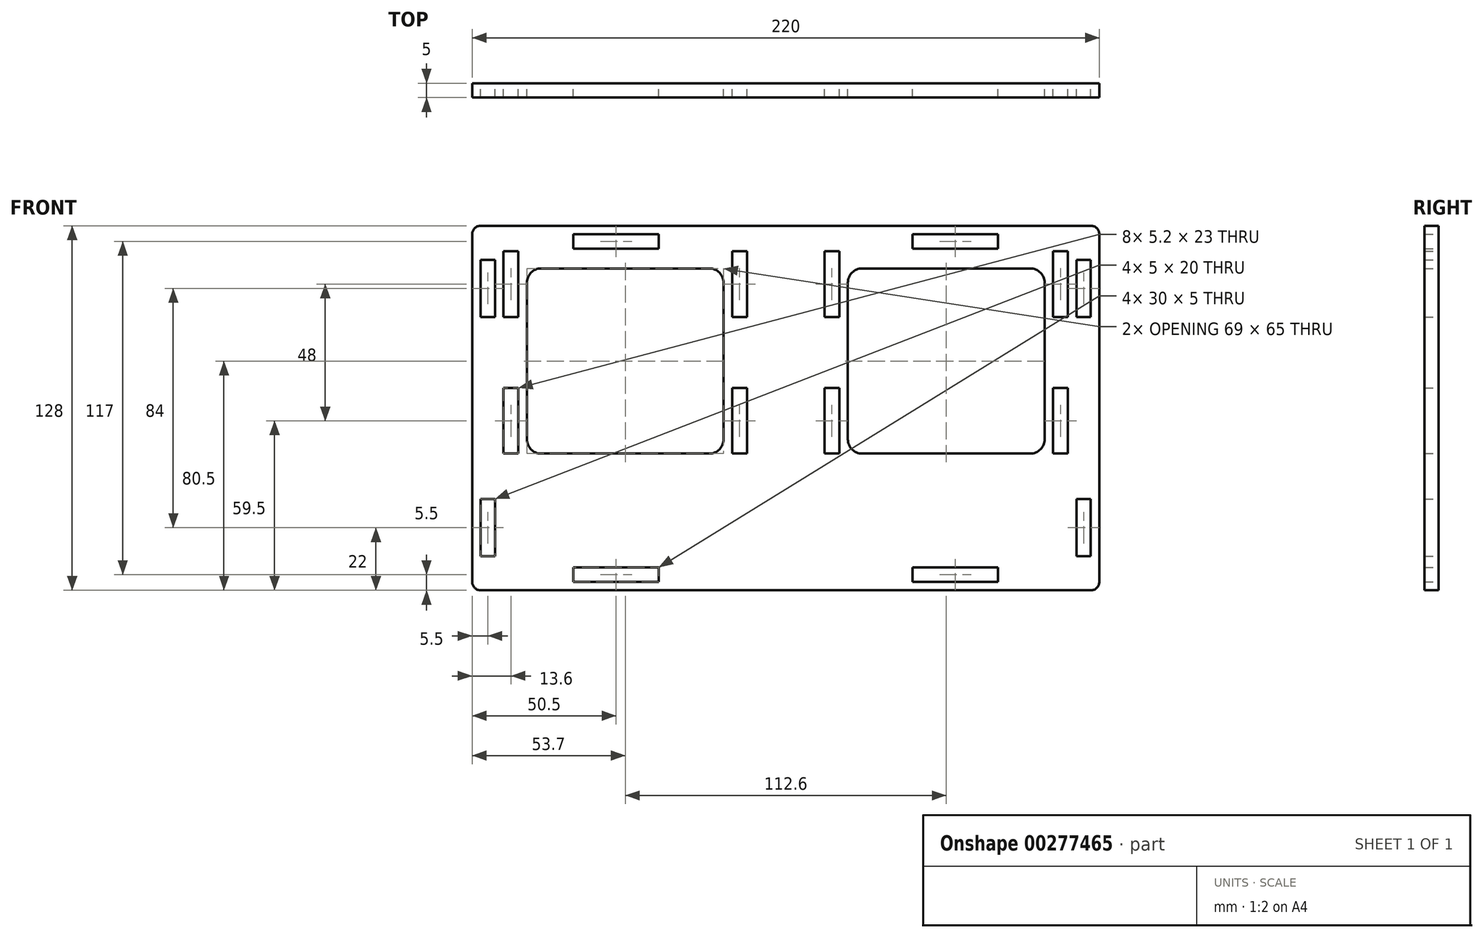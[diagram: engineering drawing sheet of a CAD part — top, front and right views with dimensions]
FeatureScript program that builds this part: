
annotation { "Feature Type Name" : "Feature", "Feature Type Description" : "" }
export const myFeature = defineFeature(function(context is Context, id is Id, definition is map)
    precondition{}
    {
        {
            var Q0;
            Q0=qCreatedBy(makeId("Front.planeOp"),FACE);
            var sketch = newSketch(context, id + "F0", { "sketchPlane" : qUnion([Q0])});
            skLineSegment(sketch, "E0.bottom", {"start": v(-107, 64) * mm, "end": v(107, 64) * mm});
            skLineSegment(sketch, "E0.top", {"start": v(-107, -64) * mm, "end": v(107, -64) * mm});
            skLineSegment(sketch, "E0.left", {"start": v(-110, 61) * mm, "end": v(-110, -61) * mm});
            skLineSegment(sketch, "E0.right", {"start": v(110, 61) * mm, "end": v(110, -61) * mm});
            skLineSegment(sketch, "E1.bottom", {"start": v(-107, 52) * mm, "end": v(-102, 52) * mm});
            skLineSegment(sketch, "E1.top", {"start": v(-107, 32) * mm, "end": v(-102, 32) * mm});
            skLineSegment(sketch, "E1.left", {"start": v(-107, 52) * mm, "end": v(-107, 32) * mm});
            skLineSegment(sketch, "E1.right", {"start": v(-102, 52) * mm, "end": v(-102, 32) * mm});
            skLineSegment(sketch, "E2.bottom", {"start": v(-107, -32) * mm, "end": v(-102, -32) * mm});
            skLineSegment(sketch, "E2.top", {"start": v(-107, -52) * mm, "end": v(-102, -52) * mm});
            skLineSegment(sketch, "E2.left", {"start": v(-107, -32) * mm, "end": v(-107, -52) * mm});
            skLineSegment(sketch, "E2.right", {"start": v(-102, -32) * mm, "end": v(-102, -52) * mm});
            skLineSegment(sketch, "E3.bottom", {"start": v(102, -32) * mm, "end": v(107, -32) * mm});
            skLineSegment(sketch, "E3.top", {"start": v(102, -52) * mm, "end": v(107, -52) * mm});
            skLineSegment(sketch, "E3.left", {"start": v(102, -32) * mm, "end": v(102, -52) * mm});
            skLineSegment(sketch, "E3.right", {"start": v(107, -32) * mm, "end": v(107, -52) * mm});
            skLineSegment(sketch, "E4.bottom", {"start": v(102, 52) * mm, "end": v(107, 52) * mm});
            skLineSegment(sketch, "E4.top", {"start": v(102, 32) * mm, "end": v(107, 32) * mm});
            skLineSegment(sketch, "E4.left", {"start": v(102, 52) * mm, "end": v(102, 32) * mm});
            skLineSegment(sketch, "E4.right", {"start": v(107, 52) * mm, "end": v(107, 32) * mm});
            skLineSegment(sketch, "E5.bottom", {"start": v(-74.5, 61) * mm, "end": v(-44.5, 61) * mm});
            skLineSegment(sketch, "E5.top", {"start": v(-74.5, 56) * mm, "end": v(-44.5, 56) * mm});
            skLineSegment(sketch, "E5.left", {"start": v(-74.5, 61) * mm, "end": v(-74.5, 56) * mm});
            skLineSegment(sketch, "E5.right", {"start": v(-44.5, 61) * mm, "end": v(-44.5, 56) * mm});
            skLineSegment(sketch, "E6.bottom", {"start": v(44.5, 61) * mm, "end": v(74.5, 61) * mm});
            skLineSegment(sketch, "E6.top", {"start": v(44.5, 56) * mm, "end": v(74.5, 56) * mm});
            skLineSegment(sketch, "E6.left", {"start": v(44.5, 61) * mm, "end": v(44.5, 56) * mm});
            skLineSegment(sketch, "E6.right", {"start": v(74.5, 61) * mm, "end": v(74.5, 56) * mm});
            skLineSegment(sketch, "E7.bottom", {"start": v(44.5, -56) * mm, "end": v(74.5, -56) * mm});
            skLineSegment(sketch, "E7.top", {"start": v(44.5, -61) * mm, "end": v(74.5, -61) * mm});
            skLineSegment(sketch, "E7.left", {"start": v(44.5, -56) * mm, "end": v(44.5, -61) * mm});
            skLineSegment(sketch, "E7.right", {"start": v(74.5, -56) * mm, "end": v(74.5, -61) * mm});
            skLineSegment(sketch, "E8.bottom", {"start": v(-74.5, -56) * mm, "end": v(-44.5, -56) * mm});
            skLineSegment(sketch, "E8.top", {"start": v(-74.5, -61) * mm, "end": v(-44.5, -61) * mm});
            skLineSegment(sketch, "E8.left", {"start": v(-74.5, -56) * mm, "end": v(-74.5, -61) * mm});
            skLineSegment(sketch, "E8.right", {"start": v(-44.5, -56) * mm, "end": v(-44.5, -61) * mm});
            skLineSegment(sketch, "E9.bottom", {"start": v(-85.8, 49) * mm, "end": v(-26.8, 49) * mm});
            skLineSegment(sketch, "E9.top", {"start": v(-85.8, -16) * mm, "end": v(-26.8, -16) * mm});
            skLineSegment(sketch, "E9.left", {"start": v(-90.8, 44) * mm, "end": v(-90.8, -11) * mm});
            skLineSegment(sketch, "E9.right", {"start": v(-21.8, 44) * mm, "end": v(-21.8, -11) * mm});
            skLineSegment(sketch, "E10.bottom", {"start": v(-18.8, 55) * mm, "end": v(-13.6, 55) * mm});
            skLineSegment(sketch, "E10.top", {"start": v(-18.8, 32) * mm, "end": v(-13.6, 32) * mm});
            skLineSegment(sketch, "E10.left", {"start": v(-18.8, 55) * mm, "end": v(-18.8, 32) * mm});
            skLineSegment(sketch, "E10.right", {"start": v(-13.6, 55) * mm, "end": v(-13.6, 32) * mm});
            skLineSegment(sketch, "E11.bottom", {"start": v(-18.8, 7) * mm, "end": v(-13.6, 7) * mm});
            skLineSegment(sketch, "E11.top", {"start": v(-18.8, -16) * mm, "end": v(-13.6, -16) * mm});
            skLineSegment(sketch, "E11.left", {"start": v(-18.8, 7) * mm, "end": v(-18.8, -16) * mm});
            skLineSegment(sketch, "E11.right", {"start": v(-13.6, 7) * mm, "end": v(-13.6, -16) * mm});
            skLineSegment(sketch, "E12.bottom", {"start": v(-99, 55) * mm, "end": v(-93.8, 55) * mm});
            skLineSegment(sketch, "E12.top", {"start": v(-99, 32) * mm, "end": v(-93.8, 32) * mm});
            skLineSegment(sketch, "E12.left", {"start": v(-99, 55) * mm, "end": v(-99, 32) * mm});
            skLineSegment(sketch, "E12.right", {"start": v(-93.8, 55) * mm, "end": v(-93.8, 32) * mm});
            skLineSegment(sketch, "E13.bottom", {"start": v(-99, 7) * mm, "end": v(-93.8, 7) * mm});
            skLineSegment(sketch, "E13.top", {"start": v(-99, -16) * mm, "end": v(-93.8, -16) * mm});
            skLineSegment(sketch, "E13.left", {"start": v(-99, 7) * mm, "end": v(-99, -16) * mm});
            skLineSegment(sketch, "E13.right", {"start": v(-93.8, 7) * mm, "end": v(-93.8, -16) * mm});
            skPoint(sketch, "E14.visualSharp", {"position": v(110, 64) * mm});
            skArc(sketch, "E14.filletArc", {"start": v(110, 61) * mm, "mid": v(109.12, 63.12) * mm, "end": v(107, 64) * mm});
            skPoint(sketch, "E15.visualSharp", {"position": v(110, -64) * mm});
            skArc(sketch, "E15.filletArc", {"start": v(107, -64) * mm, "mid": v(109.12, -63.12) * mm, "end": v(110, -61) * mm});
            skPoint(sketch, "E16.visualSharp", {"position": v(-110, -64) * mm});
            skArc(sketch, "E16.filletArc", {"start": v(-110, -61) * mm, "mid": v(-109.12, -63.12) * mm, "end": v(-107, -64) * mm});
            skPoint(sketch, "E17.visualSharp", {"position": v(-110, 64) * mm});
            skArc(sketch, "E17.filletArc", {"start": v(-107, 64) * mm, "mid": v(-109.12, 63.12) * mm, "end": v(-110, 61) * mm});
            skPoint(sketch, "E18.visualSharp", {"position": v(-21.8, 49) * mm});
            skArc(sketch, "E18.filletArc", {"start": v(-21.8, 44) * mm, "mid": v(-23.26, 47.54) * mm, "end": v(-26.8, 49) * mm});
            skPoint(sketch, "E19.visualSharp", {"position": v(-21.8, -16) * mm});
            skArc(sketch, "E19.filletArc", {"start": v(-26.8, -16) * mm, "mid": v(-23.26, -14.54) * mm, "end": v(-21.8, -11) * mm});
            skArc(sketch, "E20.filletArc", {"start": v(-90.8, -11) * mm, "mid": v(-89.34, -14.54) * mm, "end": v(-85.8, -16) * mm});
            skPoint(sketch, "E21.visualSharp", {"position": v(-90.8, 49) * mm});
            skArc(sketch, "E21.filletArc", {"start": v(-85.8, 49) * mm, "mid": v(-89.34, 47.54) * mm, "end": v(-90.8, 44) * mm});
            skLineSegment(sketch, "E22.MirrorCS", {"start": v(99, 7) * mm, "end": v(93.8, 7) * mm});
            skLineSegment(sketch, "E23.MirrorCS", {"start": v(18.8, -16) * mm, "end": v(13.6, -16) * mm});
            skLineSegment(sketch, "E24.MirrorCS", {"start": v(99, 32) * mm, "end": v(93.8, 32) * mm});
            skLineSegment(sketch, "E25.MirrorCS", {"start": v(18.8, 55) * mm, "end": v(13.6, 55) * mm});
            skLineSegment(sketch, "E26.MirrorCS", {"start": v(99, 55) * mm, "end": v(93.8, 55) * mm});
            skLineSegment(sketch, "E27.MirrorCS", {"start": v(99, -16) * mm, "end": v(93.8, -16) * mm});
            skLineSegment(sketch, "E28.MirrorCS", {"start": v(18.8, 32) * mm, "end": v(13.6, 32) * mm});
            skLineSegment(sketch, "E29.MirrorCS", {"start": v(18.8, 7) * mm, "end": v(13.6, 7) * mm});
            skArc(sketch, "E30.MirrorCS", {"start": v(26.8, -16) * mm, "mid": v(23.26, -14.54) * mm, "end": v(21.8, -11) * mm});
            skArc(sketch, "E31.MirrorCS", {"start": v(85.8, 49) * mm, "mid": v(89.34, 47.54) * mm, "end": v(90.8, 44) * mm});
            skArc(sketch, "E32.MirrorCS", {"start": v(90.8, -11) * mm, "mid": v(89.34, -14.54) * mm, "end": v(85.8, -16) * mm});
            skArc(sketch, "E33.MirrorCS", {"start": v(21.8, 44) * mm, "mid": v(23.26, 47.54) * mm, "end": v(26.8, 49) * mm});
            skLineSegment(sketch, "E34.MirrorCS", {"start": v(93.8, 7) * mm, "end": v(93.8, -16) * mm});
            skLineSegment(sketch, "E35.MirrorCS", {"start": v(21.8, 44) * mm, "end": v(21.8, -11) * mm});
            skLineSegment(sketch, "E36.MirrorCS", {"start": v(85.8, 49) * mm, "end": v(26.8, 49) * mm});
            skPoint(sketch, "E37.MirrorP", {"position": v(21.8, -16) * mm});
            skLineSegment(sketch, "E38.MirrorCS", {"start": v(90.8, 44) * mm, "end": v(90.8, -11) * mm});
            skLineSegment(sketch, "E39.MirrorCS", {"start": v(13.6, 7) * mm, "end": v(13.6, -16) * mm});
            skLineSegment(sketch, "E40.MirrorCS", {"start": v(99, 7) * mm, "end": v(99, -16) * mm});
            skLineSegment(sketch, "E41.MirrorCS", {"start": v(93.8, 55) * mm, "end": v(93.8, 32) * mm});
            skLineSegment(sketch, "E42.MirrorCS", {"start": v(99, 55) * mm, "end": v(99, 32) * mm});
            skPoint(sketch, "E43.MirrorP", {"position": v(21.8, 49) * mm});
            skLineSegment(sketch, "E44.MirrorCS", {"start": v(13.6, 55) * mm, "end": v(13.6, 32) * mm});
            skPoint(sketch, "E45.MirrorP", {"position": v(85.3, -40) * mm});
            skLineSegment(sketch, "E46.MirrorCS", {"start": v(85.8, -16) * mm, "end": v(26.8, -16) * mm});
            skLineSegment(sketch, "E47.MirrorCS", {"start": v(18.8, 7) * mm, "end": v(18.8, -16) * mm});
            skPoint(sketch, "E48.MirrorP", {"position": v(90.8, 49) * mm});
            skLineSegment(sketch, "E49.MirrorCS", {"start": v(18.8, 55) * mm, "end": v(18.8, 32) * mm});
            skLineSegment(sketch, "E50.bottom", {"start": v(-100.13, 58) * mm, "end": v(-7.43, 58) * mm, "construction": true});
            skLineSegment(sketch, "E50.top", {"start": v(-100.13, -61) * mm, "end": v(-7.43, -61) * mm, "construction": true});
            skLineSegment(sketch, "E50.left", {"start": v(-100.13, 58) * mm, "end": v(-100.13, -61) * mm, "construction": true});
            skLineSegment(sketch, "E50.right", {"start": v(-7.43, 58) * mm, "end": v(-7.43, -61) * mm, "construction": true});
            skSolve(sketch);
        }
        {
            var Q0;
            Q0=makeQuery(id+"F0.imprint","IMPRINT",FACE,{"disambiguationData":[TD([[makeQuery(id+"F0.imprint","IMPRINT",EDGE,{"derivedFrom":sQuery(id+"F0.wireOp",EDGE,"E0.bottom")}),-1.0]])]});
            extrude(context, id + "F1", {"entities" : qUnion([Q0]), "depth" : 5 * mm});
        }
    });
